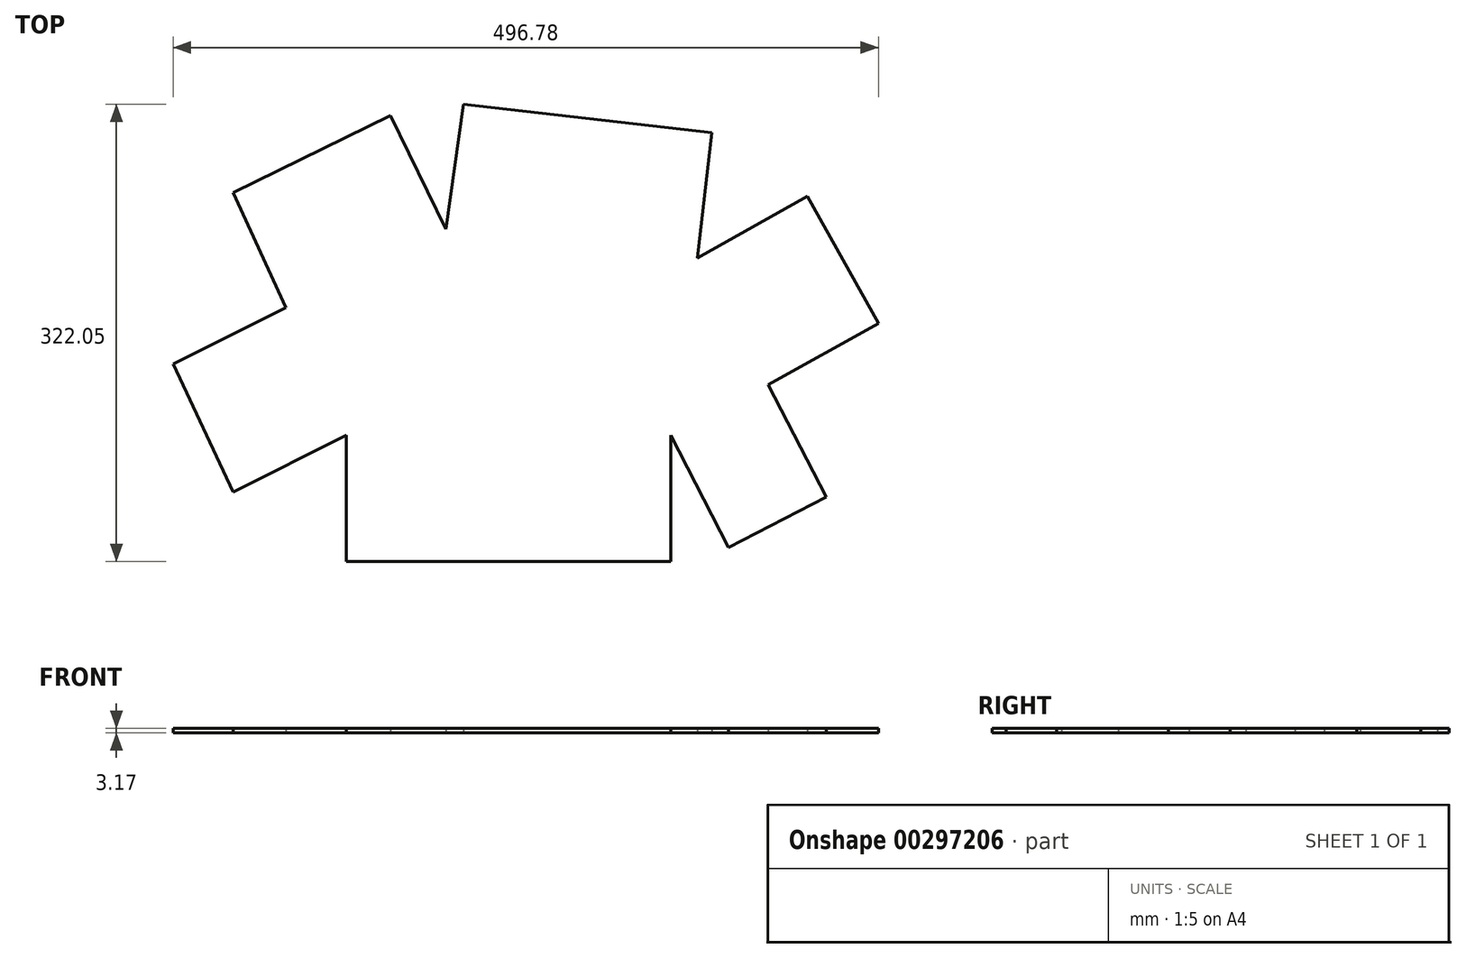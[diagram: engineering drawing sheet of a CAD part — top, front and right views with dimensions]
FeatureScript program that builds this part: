
annotation { "Feature Type Name" : "Feature", "Feature Type Description" : "" }
export const myFeature = defineFeature(function(context is Context, id is Id, definition is map)
    precondition{}
    {
        {
            var Q0;
            Q0=qCreatedBy(makeId("Top.planeOp"),FACE);
            var sketch = newSketch(context, id + "F0", { "sketchPlane" : qUnion([Q0])});
            skLineSegment(sketch, "E0", {"start": v(107.92, -16.81) * mm, "end": v(-120.68, -16.81) * mm});
            skLineSegment(sketch, "E1", {"start": v(-120.68, -16.81) * mm, "end": v(-200.1, -56.74) * mm});
            skLineSegment(sketch, "E2", {"start": v(-163.02, 73.15) * mm, "end": v(-50.37, 128.32) * mm});
            skLineSegment(sketch, "E3", {"start": v(-50.37, 128.32) * mm, "end": v(126.82, 107.92) * mm});
            skLineSegment(sketch, "E4", {"start": v(126.82, 107.92) * mm, "end": v(176.74, 18.69) * mm});
            skLineSegment(sketch, "E5", {"start": v(176.74, 18.69) * mm, "end": v(107.92, -16.81) * mm});
            skLineSegment(sketch, "E6", {"start": v(-163.02, 73.15) * mm, "end": v(-242.45, 33.23) * mm});
            skLineSegment(sketch, "E7", {"start": v(-242.45, 33.23) * mm, "end": v(-200.1, -56.74) * mm});
            skLineSegment(sketch, "E8", {"start": v(-163.02, 73.15) * mm, "end": v(-200.25, 153.88) * mm});
            skLineSegment(sketch, "E9", {"start": v(-50.37, 128.32) * mm, "end": v(-89.47, 208.16) * mm});
            skLineSegment(sketch, "E10", {"start": v(-200.25, 153.88) * mm, "end": v(-89.47, 208.16) * mm});
            skLineSegment(sketch, "E11", {"start": v(-50.37, 128.32) * mm, "end": v(-37.87, 216.34) * mm});
            skLineSegment(sketch, "E12", {"start": v(126.82, 107.92) * mm, "end": v(136.99, 196.24) * mm});
            skLineSegment(sketch, "E13", {"start": v(-37.87, 216.34) * mm, "end": v(136.99, 196.24) * mm});
            skLineSegment(sketch, "E14", {"start": v(176.74, 18.69) * mm, "end": v(254.33, 62.1) * mm});
            skLineSegment(sketch, "E15", {"start": v(126.82, 107.92) * mm, "end": v(204.4, 151.33) * mm});
            skLineSegment(sketch, "E16", {"start": v(204.4, 151.33) * mm, "end": v(254.33, 62.1) * mm});
            skLineSegment(sketch, "E17", {"start": v(176.74, 18.69) * mm, "end": v(217.5, -60.32) * mm});
            skLineSegment(sketch, "E18", {"start": v(107.92, -16.81) * mm, "end": v(148.68, -95.82) * mm});
            skLineSegment(sketch, "E19", {"start": v(217.5, -60.32) * mm, "end": v(148.68, -95.82) * mm});
            skLineSegment(sketch, "E20", {"start": v(107.92, -16.81) * mm, "end": v(107.92, -105.71) * mm});
            skLineSegment(sketch, "E21", {"start": v(-120.68, -16.81) * mm, "end": v(-120.68, -105.71) * mm});
            skLineSegment(sketch, "E22", {"start": v(-120.68, -105.71) * mm, "end": v(107.92, -105.71) * mm});
            skSolve(sketch);
        }
        {
            var Q0;
            Q0 = qSketchRegion(id + "F0", true);
            extrude(context, id + "F1", {"entities" : qUnion([Q0]), "depth" : 3.17 * mm});
        }
    });
